# Revit family: LCR
name_source: partatom
category: Lighting Fixtures
revit_build: Autodesk Revit MEP 2012 (Build: 20110916_2132(x64)
units: mm (PartAtom-declared; Revit-internal decimal feet)

## types (1)
- LCR-40HL-ED
    Apparent Load = 0 VA
    Backbox = White
    Color Filter = 16777215
    Default Elevation = 4.0'
    Description = Columbia's LCR is an LED industrial striplight with reflectors for narrow distribution and aisle lighting
    Dimming Lamp Color Temperature Shift = <None>
    Driver = 0-10V Dimming
    Emit from Line Length = 2.0'
    Glass = White Glass
    Lamp = LED Lamp
    Lumen Pkg = High Lumen
    Manufacturer = Columbia Lighting
    Manufacturer Fax = (866)-898-1065
    Model = LCR
    Nominal Watts = 56 W
    Photometric Web File = LCR-40HL-ED.ies
    Product Documentation Link = http://www.columbialighting.com
    Product Page URL = http://www.columbialighting.com
    Row Length = 4.0'
    Tilt Angle = -90.00°
    URL = http://www.columbialighting.com
    Voltage = 120 V

## geometry (parser evidence)
native form markers: Sweep x4
no freeform markers — native parametric forms only
